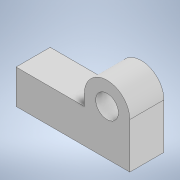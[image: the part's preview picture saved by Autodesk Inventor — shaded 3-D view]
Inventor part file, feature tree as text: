
AUTODESK INVENTOR PART (.ipt)
format: ipt  version: 2021 (Build 250183000, 183)  size: 111,616 bytes
history: native  units: mm
features: sketch x2, other x1, extrude x1, hole x1
ambient origin geometry x8: Origin, YZ Plane, XZ Plane, XY Plane, X Axis, Y Axis, Z Axis, Center Point
bodies: Body1 (feature_tree)
feature tree (5):
  other  "Sólido1"
  extrude  "Extrusão1"  Depth=40.0mm
  hole  "Furo1"  [1 undecoded]
  sketch  "Esboço1"  dims[d0=100.0mm d3=40.0mm]
  sketch  "Esboço2"  dims[d4=30.0mm d5=20.0mm d6=30.0mm d7=0.0mm d8=20.0mm d9=6.0mm d10=4.0mm d11=2.0mm d12=90.0deg d13=8.0mm d14=20.594885mm d15=0.75mm d16=20.594885mm d17=0.0625mm d18=0.75mm d19=0.375mm]
note: 1 required parameter value undecoded (feature->parameter linkage not recoverable at this tier; creation-order binding heuristic only, values carry confidence <= 0.55)
